# Revit family: Electronics_Community_Biamp_Three-Way-Full-Range-Weather-Resistant-Loudspeaker_R35-3896-EN
name_source: partatom
category: Communication Devices
units: mm (PartAtom-declared; Revit-internal decimal feet)

## family parameters
Cut with Voids When Loaded = No
Host = Face
Maintain Annotation Orientation = No
OmniClass Number = 23.85.10.11.14.14.14
OmniClass Title = Loudspeakers
Part Type = Normal
Room Calculation Point = No
Round Connector Dimension = Use Diameter
Shared = No

## types (1)
- R.35-3896-EN
    Autoformer Taps/Impedance = 25W (70V), 50W (100V) Tap: 143 Ω 50W (70V), 100W (100V) Tap: 75 Ω; 100W (70V), 200W (100V) Tap: 41 Ω 200W (70V), N/A (100V) Tap: 23 Ω
    Connector Description = NL4, 2-position terminal strip; Low Impedance 8 ohm, 70V/100V operation
    Continuous Power Handling @ Nominal Impedance = 56V; 400W @ 8 ohms (1600W peak)
    Coverage (-6dB) Horiz Vert per EN54-24 = 500Hz: 146 / 180 1 kHz: 110 / 110 ; 2 kHz: 88 / 103  4 kHz: 81 / 46
    Declared values of SPL 1-3 Oct band CPB,1W-4m, per EN54-24 (Hz dB) = 500: 69.3, 630: 69.7, 800: 69.2, 1000: 69.2,1250: 70.5, 1600: 69.1, 2000: 67.5, 2500: 70.8,3150: 69.4, 4000: 71.7
    Default Elevation = 48 "
    Depth = 13.5 "
    Description = R.35-3896-EN Three-Way Full-Range (90° x 60°) Weather-Resistant Loudspeaker
    Environmental = IP55W per IEC 60529 (with a recommended 5° down-tilt); designed to meet MIL-STD-810G standard
    Grill Material = Biamp - Plastic - Gray(Grid)
    Height = 10.98 "
    Housing Material = Biamp - Plastic - Gray
    Input Connection = NL4 Speakon-type connector for low impedance operation only; and 7-position terminal strip for low impedance or constant voltage operation
    Input Panel Weather Cover = Color-matched ABS plastic with 13.5mm ID gland nut installed in 21mm knockout
    Manufacturer = Biamp
    Model = R.35-3896-EN
    Mounting/Suspension Points = Two M8 rigging points, zinc-rich epoxy dual-layer powder-coated yoke, included integral safety cable mounting point
    Nominal Beamwidth = 90° x 60°
    Nominal Maximum SPL (Whole Space) = Music - 1m - Continuius 124 dB, Peak 130dB; 4m - Continuius 103.4; Speech - 1m - Continuius 126 dB, Peak 132dB
    Operating Environment = All Conditions, suitable for continuous outdoor direct exposure
    Operating Mode = Passive, Selectable Low Impedance or 70V/100V
    Operating Range = 95 Hz to 19 kHz
    Product Documentation Link = https://downloads.biamp.com
    Product Page URL = https://www.biamp.com
    Product data url = https://bimobject.com
    Required Accessories = Digital Signal Processor;  80 Hz 24 dB / Octave High Pass Filter
    Sensitivity = Music; 1W/1m - 98 dB, 1W/4m - 82.4 dB;  Speech; 1W/1m - 100 dB
    Shipping Weight = 40.00 lb
    Triaxial Transducers = LF  1 x 8 Carbon ring hydrophobically-treated cone, 3 VC MF 2 x 2.35 MultiSource Waveguide™ compression HF  1 x 1 exit compression
    URL = https://www.biamp.com
    Version = 1
    Weight = 34.00 lb
    Width = 12.99 "
    Yoke Material = Biamp - Metal - Gray

## geometry (parser evidence)
native form markers: Sweep x1
no freeform markers — native parametric forms only
